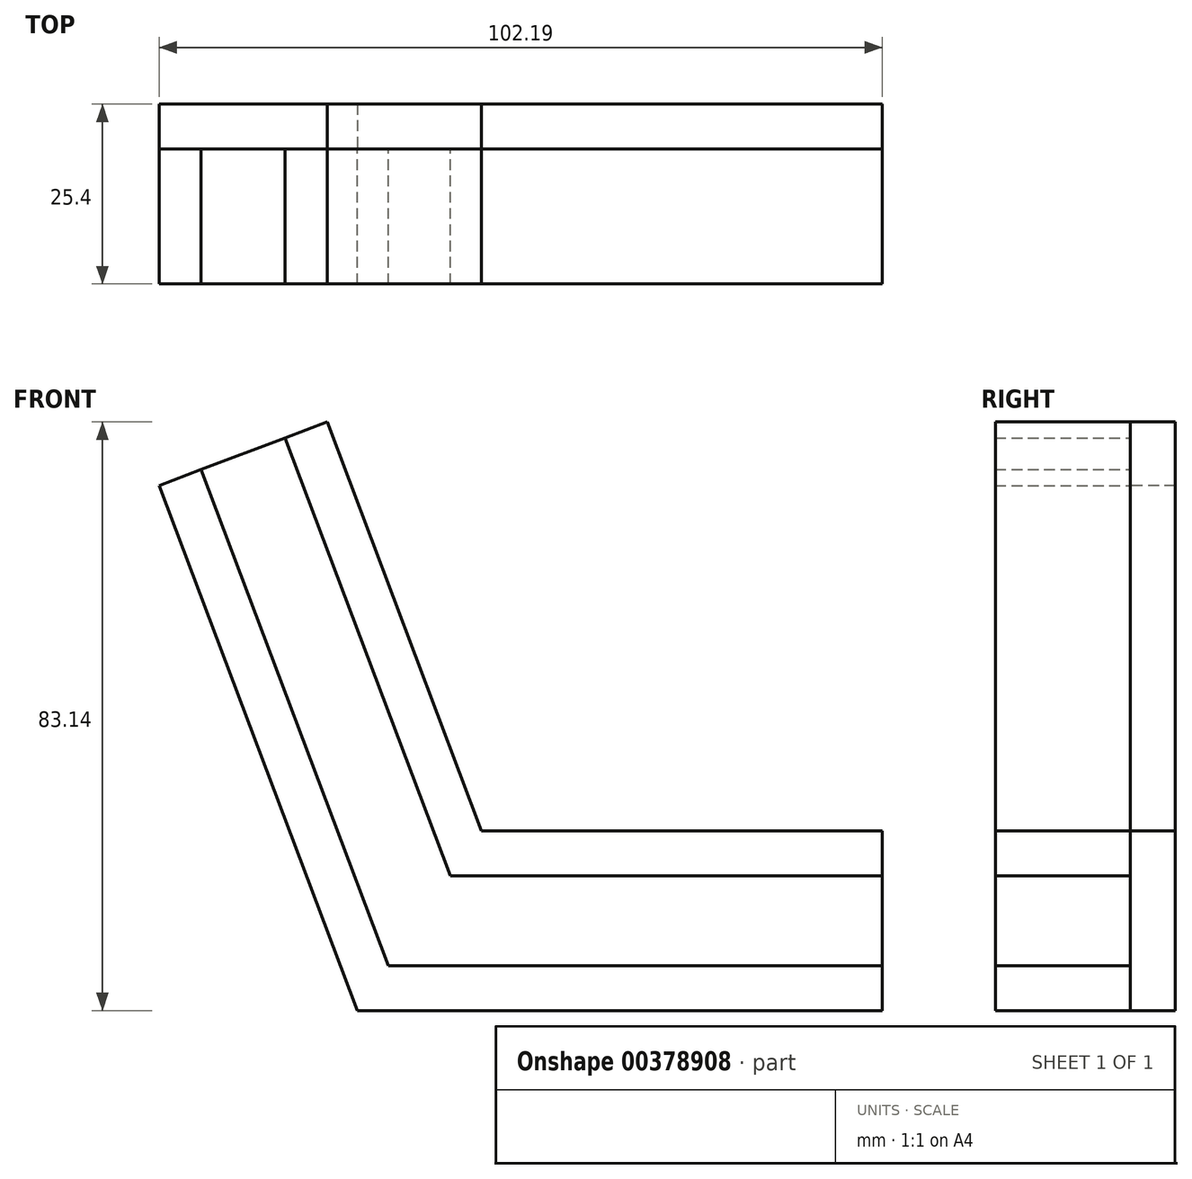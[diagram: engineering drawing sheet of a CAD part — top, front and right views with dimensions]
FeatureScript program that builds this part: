
annotation { "Feature Type Name" : "Feature", "Feature Type Description" : "" }
export const myFeature = defineFeature(function(context is Context, id is Id, definition is map)
    precondition{}
    {
        {
            var Q0;
            Q0=qCreatedBy(makeId("Front.planeOp"),FACE);
            var sketch = newSketch(context, id + "F0", { "sketchPlane" : qUnion([Q0])});
            skLineSegment(sketch, "E0", {"start": v(-21.8, 19.22) * mm, "end": v(0, -38.52) * mm});
            skLineSegment(sketch, "E1", {"start": v(0, -38.52) * mm, "end": v(56.62, -38.52) * mm});
            skLineSegment(sketch, "E2.0", {"start": v(-17.56, -63.92) * mm, "end": v(56.62, -63.92) * mm});
            skLineSegment(sketch, "E2.1", {"start": v(-45.57, 10.24) * mm, "end": v(-17.56, -63.92) * mm});
            skLineSegment(sketch, "E3", {"start": v(56.62, -63.92) * mm, "end": v(56.62, -38.52) * mm});
            skLineSegment(sketch, "E4", {"start": v(-45.57, 10.24) * mm, "end": v(-21.8, 19.22) * mm});
            skSolve(sketch);
        }
        {
            var Q0;
            Q0=qCreatedBy(makeId("Front.planeOp"),FACE);
            var sketch = newSketch(context, id + "F1", { "sketchPlane" : qUnion([Q0])});
            skLineSegment(sketch, "E5.0", {"start": v(-4.39, -44.87) * mm, "end": v(56.62, -44.87) * mm});
            skLineSegment(sketch, "E5.1", {"start": v(-27.75, 16.97) * mm, "end": v(-4.39, -44.87) * mm});
            skLineSegment(sketch, "E6.0", {"start": v(0, -38.52) * mm, "end": v(56.62, -38.52) * mm});
            skLineSegment(sketch, "E6.1", {"start": v(-21.8, 19.22) * mm, "end": v(0, -38.52) * mm});
            skLineSegment(sketch, "E7", {"start": v(-21.8, 19.22) * mm, "end": v(-27.75, 16.97) * mm});
            skLineSegment(sketch, "E8", {"start": v(56.62, -38.52) * mm, "end": v(56.62, -44.87) * mm});
            skSolve(sketch);
        }
        {
            var Q0;
            Q0 = qSketchRegion(id + "F1", true);
            extrude(context, id + "F2", {"entities" : qUnion([Q0]), "depth" : 19.05 * mm});
        }
        {
            var Q0;
            Q0=qCreatedBy(makeId("Front.planeOp"),FACE);
            var sketch = newSketch(context, id + "F3", { "sketchPlane" : qUnion([Q0])});
            skLineSegment(sketch, "E9.0", {"start": v(-13.17, -57.57) * mm, "end": v(56.62, -57.57) * mm});
            skLineSegment(sketch, "E9.1", {"start": v(-39.63, 12.49) * mm, "end": v(-13.17, -57.57) * mm});
            skLineSegment(sketch, "E10.0", {"start": v(-17.56, -63.92) * mm, "end": v(56.62, -63.92) * mm});
            skLineSegment(sketch, "E10.1", {"start": v(-45.57, 10.24) * mm, "end": v(-17.56, -63.92) * mm});
            skLineSegment(sketch, "E11", {"start": v(-45.57, 10.24) * mm, "end": v(-39.63, 12.49) * mm});
            skLineSegment(sketch, "E12", {"start": v(56.62, -57.57) * mm, "end": v(56.62, -63.92) * mm});
            skSolve(sketch);
        }
        {
            var Q0;
            Q0 = qSketchRegion(id + "F3", true);
            extrude(context, id + "F4", {"entities" : qUnion([Q0]), "depth" : 19.05 * mm});
        }
        {
            var Q0;
            Q0=makeQuery(id+"F0.imprint","IMPRINT",FACE,{"disambiguationData":[TD([[makeQuery(id+"F0.imprint","IMPRINT",EDGE,{"derivedFrom":sQuery(id+"F0.wireOp",EDGE,"E0")}),-1.0]])]});
            extrude(context, id + "F5", {"entities" : qUnion([Q0]), "oppositeDirection" : true, "depth" : 6.35 * mm});
        }
    });
